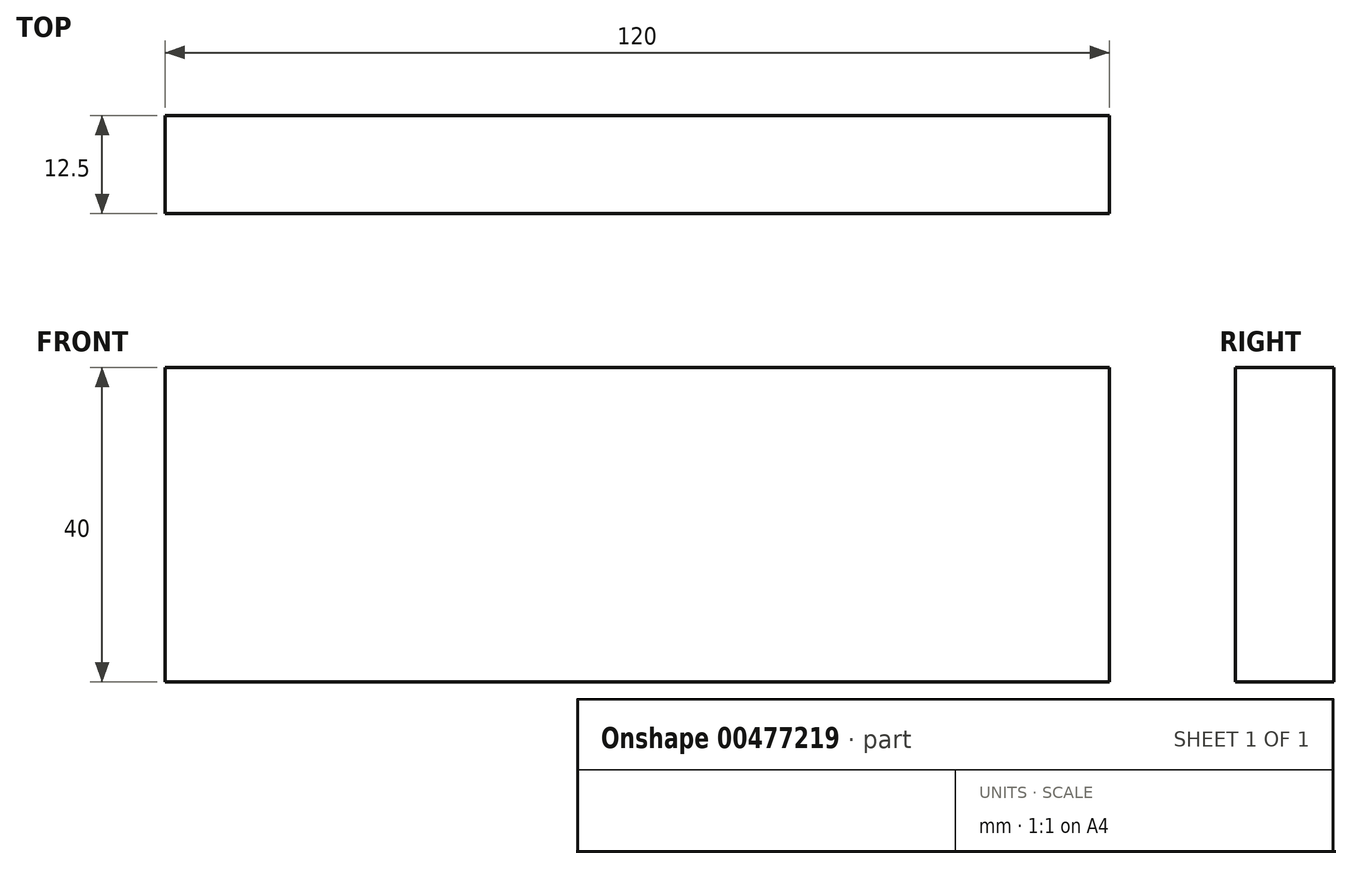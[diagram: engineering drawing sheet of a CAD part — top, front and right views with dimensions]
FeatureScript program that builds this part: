
annotation { "Feature Type Name" : "Feature", "Feature Type Description" : "" }
export const myFeature = defineFeature(function(context is Context, id is Id, definition is map)
    precondition{}
    {
        {
            var Q0;
            Q0=qCreatedBy(makeId("Right.planeOp"),FACE);
            var sketch = newSketch(context, id + "F0", { "sketchPlane" : qUnion([Q0])});
            skLineSegment(sketch, "E0", {"start": v(0, 0) * mm, "end": v(0, -40) * mm});
            skLineSegment(sketch, "E1.top", {"start": v(-25, -40) * mm, "end": v(0, -40) * mm});
            skLineSegment(sketch, "E1.left", {"start": v(-25, 0) * mm, "end": v(-25, -40) * mm});
            skLineSegment(sketch, "E2", {"start": v(-12.5, 2.93) * mm, "end": v(-12.5, -40) * mm});
            skLineSegment(sketch, "E3", {"start": v(0, 0) * mm, "end": v(-12.5, 0) * mm});
            skSolve(sketch);
        }
        {
            var Q0;
            {var subQ0=sQuery(id+"F0.wireOp",EDGE,"E0");Q0=makeQuery(id+"F0.imprint","IMPRINT",FACE,{"disambiguationData":[TD([[makeQuery(id+"F0.imprint","IMPRINT",EDGE,{"derivedFrom":subQ0}),-1.0]])]});}
            extrude(context, id + "F1", {"entities" : qUnion([Q0]), "endBound" : BoundingType.SYMMETRIC, "depth" : 120 * mm});
        }
    });
